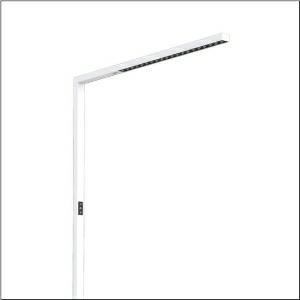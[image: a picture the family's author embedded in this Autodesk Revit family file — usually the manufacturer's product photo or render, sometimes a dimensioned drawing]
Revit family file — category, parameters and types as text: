
# Revit family: silica_r__31_floor_51my52fa4cw_1f6d
name_source: partatom
category: Lighting Fixtures
units: mm (PartAtom-declared; Revit-internal decimal feet)

## family parameters
Cut with Voids When Loaded = No
Host = Face
Light Source = No
Part Type = Normal
Room Calculation Point = No
Round Connector Dimension = Use Diameter
Shared = No

## types (1)
- Silica® 31 Floor (1 x LED, 10600 lm, 75 W, 4000K)
    Apparent Load = 75 VA
    CIE Flux Codes = 86 100 100 24 100
    Color Rendering = 80
    Color Temperature = 4000K
    Default Elevation = 1800 mm
    Description = Silica® 31 Floor, floorstanding luminaire, secondary optical cover: cover panel, of PMMA, light emission: direct/indirect distribution, primary light characteristic: symmetric, installation type: not mounted, LED, rated luminous flux: 10.600lm, luminous efficacy: 141lm/W, light colour: 840, colour temperature: 4000K, control gear: Touchdim, daylight-dependent control, with cable with plug, mains connection: 230V, AC, 50Hz, connection cable pre-assembled, rated input power: 75W, luminaire head, of aluminium, traffic white (RAL 9016), length: 1.203mm, width: 52mm, supporting column, angular, of aluminium, traffic white (RAL 9016), baseplate, of steel, traffic white (RAL 9016), protection rating (complete): IP20, insulation class (complete): insulation class I (protective earthing), certification: CE, permissible operating ambient temperature: -20..+40°C, standard: EN 50419, packaging unit: 1 piece
    Height = 36 mm
    Lamp = 1 x LED
    Lamp Light Flux = 10600 lm
    Lamp Power = 75 W
    Lamp count = 1
    Length = 1203 mm
    Luminous efficacy = 141 lm/W
    Manufacturer = Siteco
    ModVariant = No
    Model = 51MY52FA4CW
    Mounting Place = Floor
    Mounting Type = Freestanding
    Number of Poles = 1
    OnlyDefault = Yes
    Power Factor = 1
    Product Name = Silica® 31 Floor
    Product group = floorstanding luminaire
    ProductGroupID = 1302
    Protection Class = Protection class I
    Protection Degree = IP 20
    RLX_Detail_Level = 1
    RLX_Emergency_Light_Flux = 0 lm
    RLX_Emergency_Type = 0
    RLX_Emergency_Type_DB = No
    RlxData = <blob elided: 17149 chars, md5=23d51dd0>
    Socket = socket
    Standby Power = 0 W
    System Light Flux = 10600 lm
    System Power = 75 W
    Type Comments = Product without accessories
    Type Image = l_1275309.jpg
    URL = http://relux.com
    VarID = ---
    Voltage = 0 V
    Weight = 0.00 kg
    Width = 52 mm  [stored 0.170604 ft]

note: [stored X ft] marks values corroborated as IEEE doubles in the binary element streams (Revit-internal decimal feet)

## geometry (parser evidence)
native form markers: Blend x4, Sweep x13
no freeform markers — native parametric forms only
